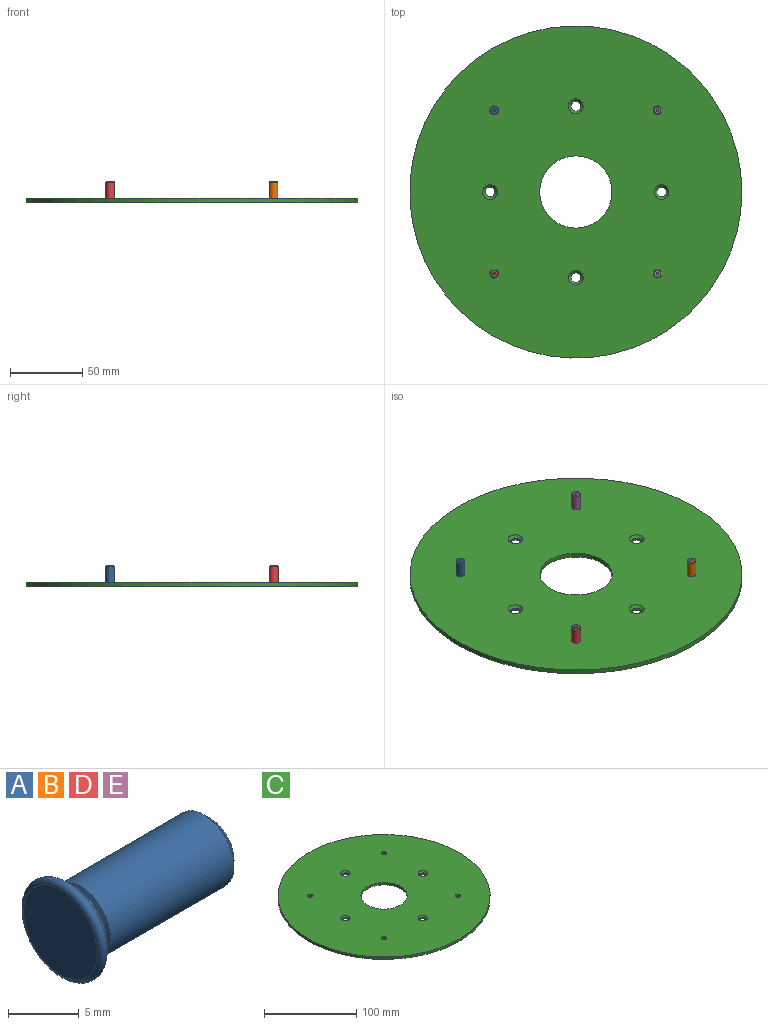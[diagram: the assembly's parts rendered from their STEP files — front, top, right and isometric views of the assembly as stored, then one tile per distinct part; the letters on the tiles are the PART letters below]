
ASSEMBLY  parts=5 mates=4
PART A: 13 faces, bbox 15x8.9x8.9 mm
  f0: cone r=0.45mm half-angle=60deg, axis (1,0,0), area 2.9mm2, adj f1
  f1: plane 4.77x4.77mm, normal (1,0,0), area 15.3mm2, adj f0,f2
  f2: cone r=2.69mm half-angle=45deg, axis (-1,0,0), area 14.7mm2, adj f1,f3
  f3: cylinder r=3mm len=12.39mm, axis (-1,0,0), area 233.5mm2, adj f2,f4
  f4: cone r=2.85mm half-angle=63.4deg, axis (1,0,0), area 6mm2, adj f3,f5
  f5: torus R=2.83mm, axis (-1,0,0), area 2.7mm2, adj f4,f6
  f6: cone r=2.85mm half-angle=63.4deg, axis (-1,0,0), area 6mm2, adj f5,f7
  f7: cylinder r=3mm len=6mm, axis (-1,0,0), area 6mm2, adj f6,f8
  f8: plane 6.97x6.97mm, normal (1,0,0), area 9.9mm2, adj f7,f9
  f9: cylinder r=3.48mm len=6.97mm, axis (1,0,0), area 9mm2, adj f8,f12
  f10: plane 7.38x7.38mm, normal (-1,0,0), area 42.8mm2, adj f11
  f11: torus R=3.69mm, axis (-1,0,0), area 32mm2, adj f10,f12
  f12: plane 7.38x7.38mm, normal (1,0,0), area 4.6mm2, adj f9,f11
PART B: same geometry as A
PART C: 16 faces, bbox 230x230x3.2 mm
  f0: cylinder r=3mm len=6mm, axis (0,0,1), area 59.8mm2, adj f11,f12
  f1: cylinder r=3mm len=6mm, axis (0,0,1), area 59.8mm2, adj f11,f12
  f2: cylinder r=3mm len=6mm, axis (0,0,1), area 59.8mm2, adj f11,f12
  f3: cylinder r=3.4mm len=6.8mm, axis (0,0,1), area 31.4mm2, adj f4,f12
  f4: cone r=3.4mm half-angle=45deg, axis (0,0,1), area 64.5mm2, adj f3,f11
  f5: cylinder r=3.4mm len=6.8mm, axis (0,0,1), area 31.4mm2, adj f6,f12
  f6: cone r=3.4mm half-angle=45deg, axis (0,0,1), area 64.5mm2, adj f5,f11
  f7: cylinder r=3.4mm len=6.8mm, axis (0,0,1), area 31.4mm2, adj f8,f12
  f8: cone r=3.4mm half-angle=45deg, axis (0,0,1), area 64.5mm2, adj f7,f11
  f9: cylinder r=25mm len=50mm, axis (0,0,-1), area 498.7mm2, adj f11,f12
  f10: cylinder r=115mm len=230mm, axis (0,0,-1), area 2294.1mm2, adj f11,f12
  f11: plane 230x230mm, normal (0,0,1), area 39143.2mm2, adj f0,f1,f2,f4,f6,f8,f9,f10
  f12: plane 230x230mm, normal (0,0,-1), area 39325.7mm2, adj f0,f1,f2,f3,f5,f7,f9,f10
  f13: cylinder r=3.4mm len=6.8mm, axis (0,0,1), area 31.4mm2, adj f12,f14
  f14: cone r=3.4mm half-angle=45deg, axis (0,0,1), area 64.5mm2, adj f11,f13
  f15: cylinder r=3mm len=6mm, axis (0,0,1), area 59.8mm2, adj f11,f12
PART D: same geometry as A
PART E: same geometry as A
PLACE A rot(axis=(0,-1,0),90deg) t=(-120.03,32.7,12.66)mm
PLACE B rot(axis=(0,-1,0),90deg) t=(-6.9,-80.44,12.66)mm
PLACE C t=(-63.47,-23.87,12.66)mm
PLACE D rot(axis=(0,-1,0),90deg) t=(-120.03,-80.44,12.66)mm
PLACE E rot(axis=(0,-1,0),90deg) t=(-6.9,32.7,12.66)mm
MATE cylindrical B.f3 <-> C.f0  axis (0,0,-1) through (-6.9,-80.44,12.66)mm
MATE cylindrical D.f3 <-> C.f1  axis (0,0,-1) through (-120.03,-80.44,12.66)mm
MATE cylindrical A.f3 <-> C.f2  axis (0,0,-1) through (-120.03,32.7,12.66)mm
MATE cylindrical E.f3 <-> C.f15  axis (0,0,-1) through (-6.9,32.7,12.66)mm
